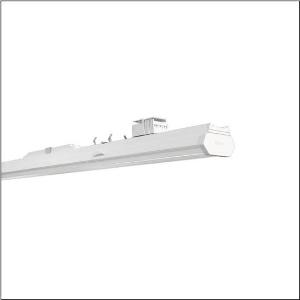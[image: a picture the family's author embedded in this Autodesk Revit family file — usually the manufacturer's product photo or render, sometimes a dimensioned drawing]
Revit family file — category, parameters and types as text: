
# Revit family: licross_r__21_protected_mo_52td127n485g_89bf
name_source: partatom
category: Lighting Fixtures
units: mm (PartAtom-declared; Revit-internal decimal feet)

## family parameters
Cut with Voids When Loaded = No
Host = Face
Light Source = No
Part Type = Normal
Room Calculation Point = No
Round Connector Dimension = Use Diameter
Shared = No

## types (1)
- Licross® 21 Protected MO (1 x LED, 8610 lm, 47.9 W, 4000K)
    Apparent Load = 48 VA
    CIE Flux Codes = 73 92 98 99 100
    Color Rendering = 80
    Color Temperature = 4000K
    Default Elevation = 1800 mm
    Description = Licross® 21 Protected MO, luminaire insert, of sheet steel, galvanised, coil coated, white, length: 1.500mm, width: 90mm, height: 101mm, LED rated luminous flux: 8.610lm, light colour: 840, control gear: ON/OFF, with plug, 3-pole, with phase selection, mains connection: 220..240V, AC, 50/60Hz, rated input power: 48W, halogen-free wiring, primary light control with lens, of plastic, primary optical cover: cover, of PMMA, light emission: direct distribution, primary light characteristic: symmetric, protection rating (complete): IP54, insulation class (complete): insulation class I (protective earthing), certification: CE, ENEC, VDE, UKCA, protection symbol: D if used in an environment with non-conductive dust loads with corresponding accessories, impact resistance: IK06, permissible ambient temperature for indoor applications: -35..+45°C, corresponds to IFS (International Featured Standards) requirements for safety and quality in the food industry, reducing of maximum allowable ambient temperature of 5°C with ceiling mounting, LABS conformity tested according to VDMA 24364:2018-05, packaging unit: 1 piece
    Height = 92 mm
    Lamp = 1 x LED
    Lamp Light Flux = 8610 lm
    Lamp Power = 47.9 W
    Lamp count = 1
    Length = 1500 mm
    Luminous efficacy = 180 lm/W
    Manufacturer = Siteco
    ModVariant = No
    Model = 52TD127N485G
    Mounting Place = Ceiling
    Mounting Type = Pendant
    Number of Poles = 1
    OnlyDefault = Yes
    Power Factor = 1
    Product Name = Licross® 21 Protected MO
    Product group = luminaire insert
    ProductGroupID = 901
    Protection Class = Protection class I
    Protection Degree = IP 54
    RLX_Detail_Level = 1
    RLX_Emergency_Light_Flux = 0 lm
    RLX_Emergency_Type = 0
    RLX_Emergency_Type_DB = No
    RlxData = <blob elided: 20701 chars, md5=5965ac5f>
    Socket = socket
    Standby Power = 0 W
    System Light Flux = 8610 lm
    System Power = 48 W
    Type Comments = Product without accessories
    Type Image = l_1256148.jpg
    URL = http://relux.com
    VarID = ---
    Voltage = 0 V
    Weight = 0.00 kg
    Width = 88 mm

## geometry (parser evidence)
native form markers: Blend x4, Sweep x10
no freeform markers — native parametric forms only
